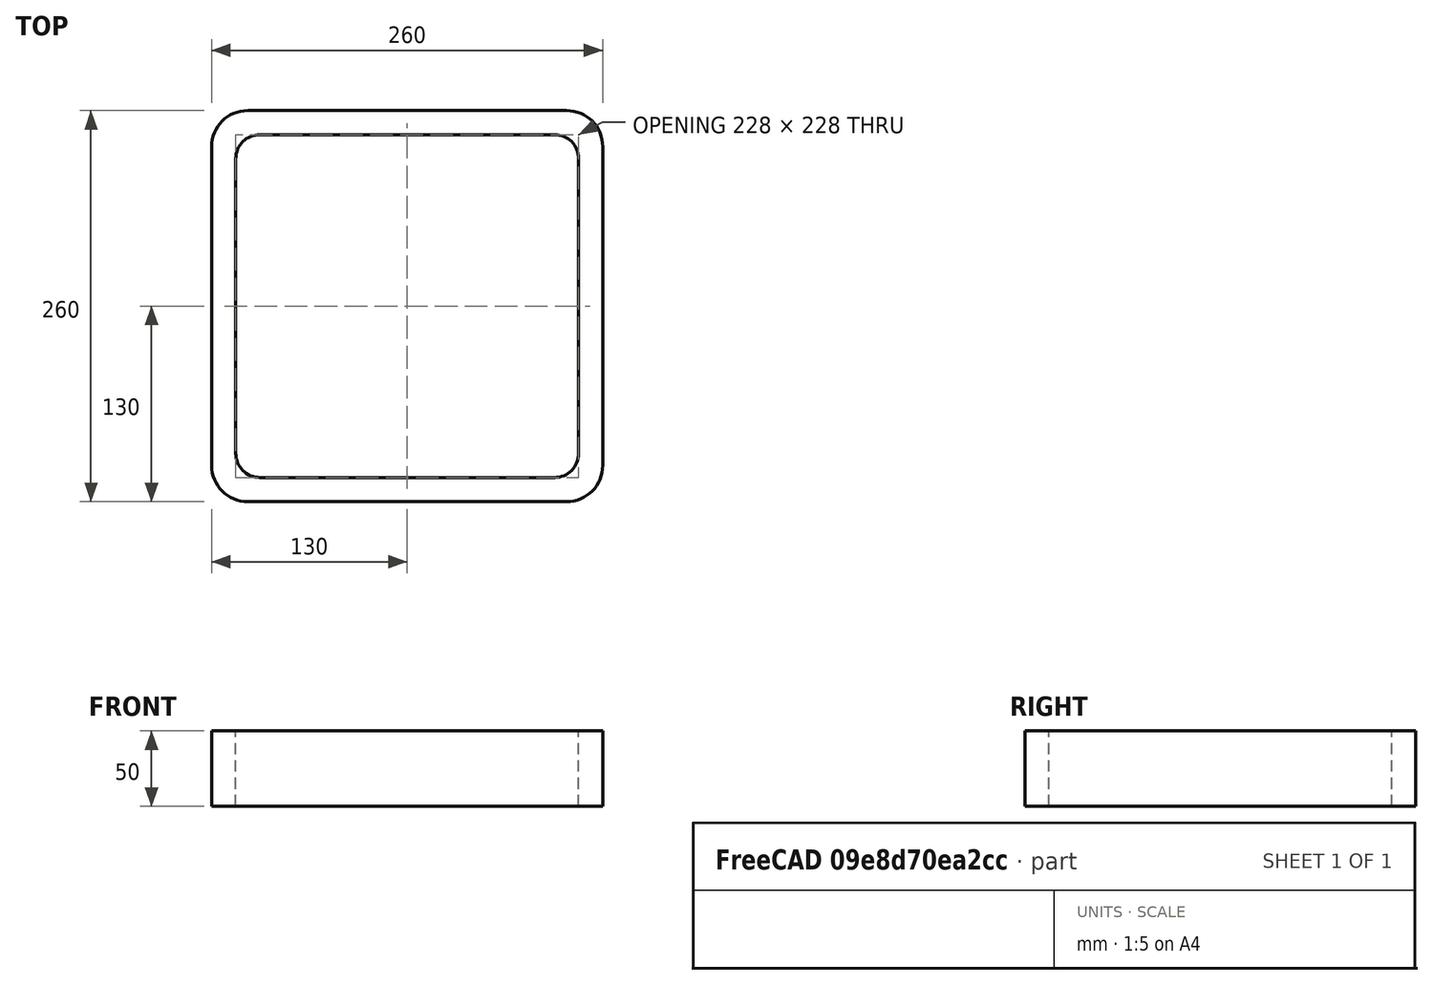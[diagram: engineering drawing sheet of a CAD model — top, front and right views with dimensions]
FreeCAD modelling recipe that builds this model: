
FCSTD DOCUMENT  (FreeCAD 0.15R4671 (Git))
Label: Square hollow section 260x260x16 EN10219 S235JRH
License: All rights reserved
LicenseURL: http://en.wikipedia.org/wiki/All_rights_reserved
objects: Sketcher::SketchObject×1, Part::Extrusion×1
note: 2 computed .brp shape members not serialized (recipe doc carries the construction recipe); baked Part::Feature solids carry a one-line shape summary decoded from their .brp

FEATURE [Sketcher::SketchObject] Sketch
  sketch-geometry (16):
    g0: LineSegment StartX=-98 StartY=114 StartZ=0 EndX=98 EndY=114 EndZ=0
    g1: LineSegment StartX=114 StartY=98 StartZ=0 EndX=114 EndY=-98 EndZ=0
    g2: LineSegment StartX=98 StartY=-114 StartZ=0 EndX=-98 EndY=-114 EndZ=0
    g3: LineSegment StartX=-114 StartY=-98 StartZ=0 EndX=-114 EndY=98 EndZ=0
    g4: LineSegment StartX=-106 StartY=130 StartZ=0 EndX=106 EndY=130 EndZ=0
    g5: LineSegment StartX=130 StartY=106 StartZ=0 EndX=130 EndY=-106 EndZ=0
    g6: LineSegment StartX=106 StartY=-130 StartZ=0 EndX=-106 EndY=-130 EndZ=0
    g7: LineSegment StartX=-130 StartY=-106 StartZ=0 EndX=-130 EndY=106 EndZ=0
    g8: ArcOfCircle CenterX=-98 CenterY=98 CenterZ=0 NormalX=0 NormalY=0 NormalZ=1 Radius=16 StartAngle=1.5708 EndAngle=3.14159
    g9: ArcOfCircle CenterX=98 CenterY=98 CenterZ=0 NormalX=0 NormalY=0 NormalZ=1 Radius=16 StartAngle=0 EndAngle=1.5708
    g10: ArcOfCircle CenterX=98 CenterY=-98 CenterZ=0 NormalX=0 NormalY=0 NormalZ=1 Radius=16 StartAngle=4.71239 EndAngle=6.28319
    g11: ArcOfCircle CenterX=-98 CenterY=-98 CenterZ=0 NormalX=0 NormalY=0 NormalZ=1 Radius=16 StartAngle=3.14159 EndAngle=4.71239
    g12: ArcOfCircle CenterX=106 CenterY=106 CenterZ=0 NormalX=0 NormalY=0 NormalZ=1 Radius=24 StartAngle=0 EndAngle=1.5708
    g13: ArcOfCircle CenterX=106 CenterY=-106 CenterZ=0 NormalX=0 NormalY=0 NormalZ=1 Radius=24 StartAngle=4.71239 EndAngle=6.28319
    g14: ArcOfCircle CenterX=-106 CenterY=-106 CenterZ=0 NormalX=0 NormalY=0 NormalZ=1 Radius=24 StartAngle=3.14159 EndAngle=4.71239
    g15: ArcOfCircle CenterX=-106 CenterY=106 CenterZ=0 NormalX=0 NormalY=0 NormalZ=1 Radius=24 StartAngle=1.5708 EndAngle=3.14159
  constraints (36):
    c: Horizontal(g2)
    c: Vertical(g3)
    c: Horizontal(g6)
    c: Vertical(g7)
    c: Tangent(g3,g8) = 1.5708
    c: Tangent(g0,g8) = 1.5708
    c: Tangent(g0,g9) = 1.5708
    c: Tangent(g1,g9) = 1.5708
    c: Tangent(g1,g10) = 1.5708
    c: Tangent(g2,g10) = 1.5708
    c: Tangent(g2,g11) = 1.5708
    c: Tangent(g3,g11) = 1.5708
    c: Tangent(g4,g12) = 1.5708
    c: Tangent(g5,g12) = 1.5708
    c: Tangent(g5,g13) = 1.5708
    c: Tangent(g6,g13) = 1.5708
    c: Tangent(g6,g14) = 1.5708
    c: Tangent(g7,g14) = 1.5708
    c: Tangent(g7,g15) = 1.5708
    c: Tangent(g4,g15) = 1.5708
    c: Equal(g9,g8)
    c: Equal(g9,g11)
    c: Equal(g9,g10)
    c: Equal(g12,g15)
    c: Equal(g12,g14)
    c: Equal(g12,g13)
    c: Symmetric(g4,g6,g-1)
    c: Symmetric(g7,g5,g-2)
    c: DistanceY(g4,g6) = -260
    c: DistanceX(g7,g5) = 260
    c: Symmetric(g3,g1,g-2)
    c: Symmetric(g0,g2,g-1)
    c: DistanceY(g0,g4) = 16
    c: DistanceX(g5,g1) = -16
    c: Radius(g9) = 16
    c: Radius(g12) = 24
FEATURE [Part::Extrusion] Extrude  label="Square hollow section 260x260x16 EN10219 S235JRH"
  Base = -> Sketch
  Dir = (0,0,50)
  Solid = true
